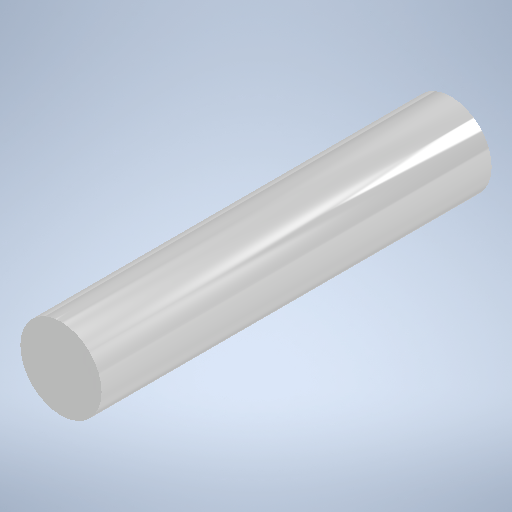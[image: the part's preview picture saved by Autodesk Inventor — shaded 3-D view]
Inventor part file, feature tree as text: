
AUTODESK INVENTOR PART (.ipt)
format: ipt  version: 2025 (Build 290162010, 162A)  size: 250,880 bytes
history: native  units: mm
features: extrude x1, plane x1, sketch x1
ambient origin geometry x8: Origin, YZ Plane, XZ Plane, XY Plane, X Axis, Y Axis, Z Axis, Center Point
bodies: Volumenkörper1 (feature_tree)
feature tree (3):
  extrude  "Extrusion1"  Depth=24.0mm TaperAngle=0.0deg
  plane  "Work Plane1"
  sketch  "Skizze1"  dims[d0=5.0mm d1=24.0mm d2=0.0mm]
